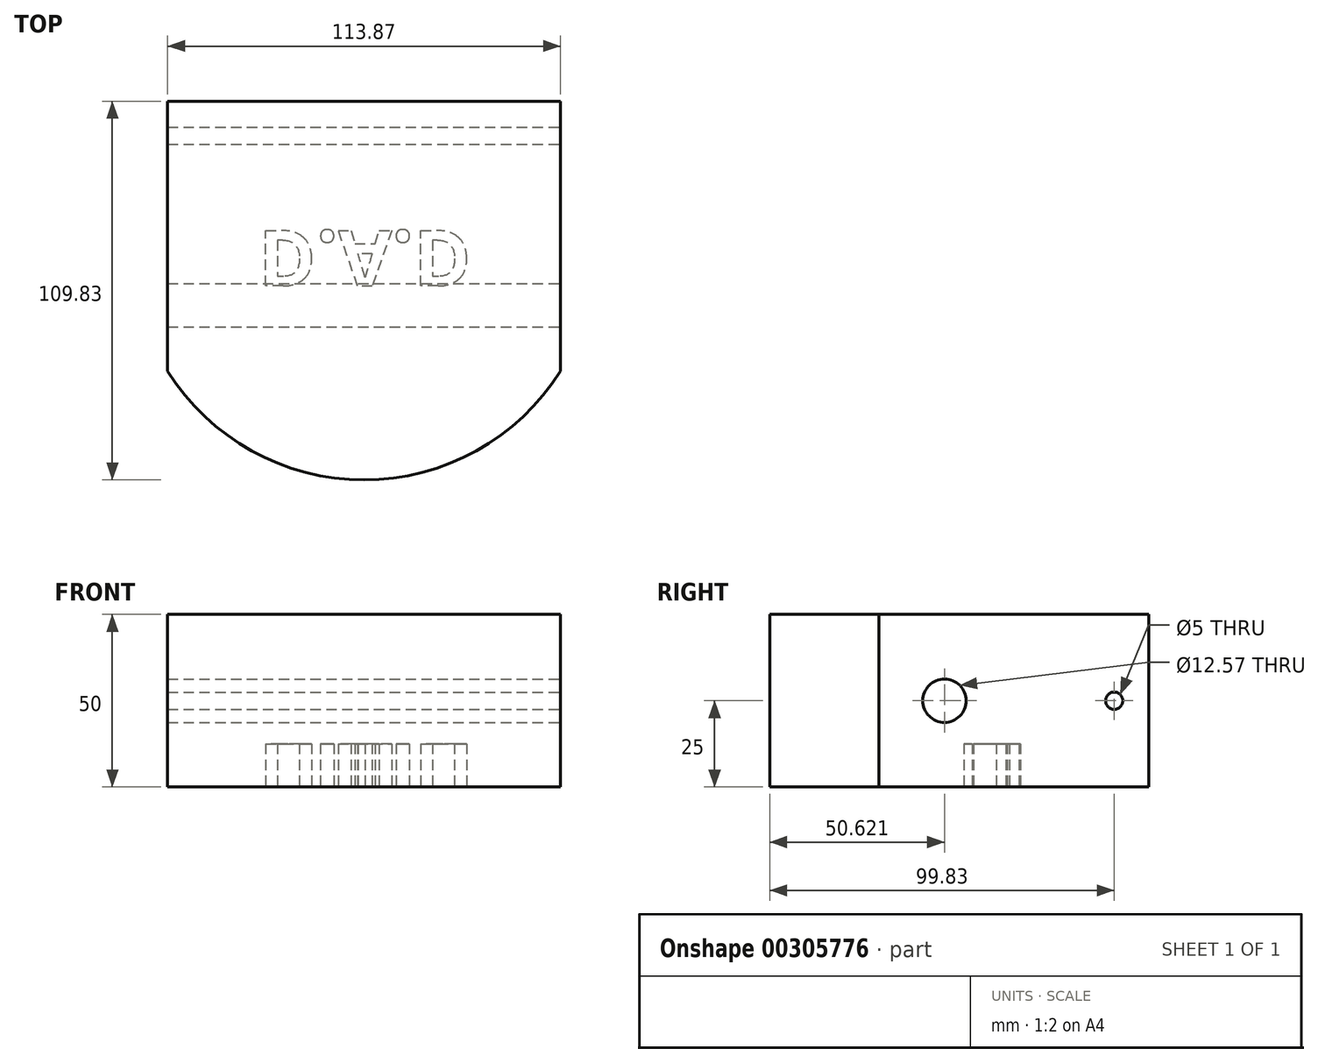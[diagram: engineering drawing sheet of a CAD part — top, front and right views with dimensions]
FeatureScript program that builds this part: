
annotation { "Feature Type Name" : "Feature", "Feature Type Description" : "" }
export const myFeature = defineFeature(function(context is Context, id is Id, definition is map)
    precondition{}
    {
        {
            var Q0;
            Q0=qCreatedBy(makeId("Top.planeOp"),FACE);
            var sketch = newSketch(context, id + "F0", { "sketchPlane" : qUnion([Q0])});
            skLineSegment(sketch, "E0.bottom", {"start": v(56.58, -32.5) * mm, "end": v(-57.29, -32.5) * mm});
            skLineSegment(sketch, "E0.top", {"start": v(56.58, 45.78) * mm, "end": v(-57.29, 45.78) * mm});
            skLineSegment(sketch, "E0.left", {"start": v(56.58, -32.5) * mm, "end": v(56.58, 45.78) * mm});
            skLineSegment(sketch, "E0.right", {"start": v(-57.29, -32.5) * mm, "end": v(-57.29, 45.78) * mm});
            skArc(sketch, "E1", {"start": v(-57.29, -32.5) * mm, "mid": v(-0.35, -64.05) * mm, "end": v(56.58, -32.5) * mm});
            skSolve(sketch);
        }
        {
            var Q0;
            Q0 = qSketchRegion(id + "F0", true);
            extrude(context, id + "F1", {"entities" : qUnion([Q0]), "depth" : 50 * mm});
        }
        {
            var Q0;
            Q0=makeQuery(id+"F1.opExtrude","SWEPT_FACE",FACE,{"disambiguationData":[OSD([sQuery(id+"F0.wireOp",EDGE,"E0.left")])]});
            var sketch = newSketch(context, id + "F2", { "sketchPlane" : qUnion([Q0])});
            skLineSegment(sketch, "E2", {"start": v(45.78, 25) * mm, "end": v(-32.5, 25) * mm, "construction": true});
            skCircle(sketch, "E3", {"center": v(35.78, 25) * mm, "radius": 2.5 * mm});
            skCircle(sketch, "E4", {"center": v(-13.43, 25) * mm, "radius": 6.29 * mm});
            skSolve(sketch);
        }
        {
            var Q0;
            Q0=makeQuery(id+"F2.imprint","IMPRINT",FACE,{"disambiguationData":[TD([[makeQuery(id+"F2.imprint","IMPRINT",EDGE,{"derivedFrom":sQuery(id+"F2.wireOp",EDGE,"E4")}),1.0]])]});
            var Q1;
            Q1=makeQuery(id+"F2.imprint","IMPRINT",FACE,{"disambiguationData":[TD([[makeQuery(id+"F2.imprint","IMPRINT",EDGE,{"derivedFrom":sQuery(id+"F2.wireOp",EDGE,"E3")}),1.0]])]});
            extrude(context, id + "F3", {"entities" : qUnion([Q0, Q1]), "operationType" : NewBodyOperationType.REMOVE, "endBound" : BoundingType.THROUGH_ALL, "oppositeDirection" : true, "depth" : 25 * mm});
        }
        {
            var Q0;
            Q0=makeQuery(id+"F1.opExtrude","CAP_FACE",FACE,{"disambiguationData":[OSD([sQuery(id+"F0.wireOp",EDGE,"E0.top"),sQuery(id+"F0.wireOp",EDGE,"E0.left"),sQuery(id+"F0.wireOp",EDGE,"E0.right"),sQuery(id+"F0.wireOp",EDGE,"E1")])],"isStart":true});
            var sketch = newSketch(context, id + "F4", { "sketchPlane" : qUnion([Q0])});
            skText(sketch, "E5", { "text": "D.A.D", "fontName": "OpenSans-Bold.ttf"});
            skLineSegment(sketch, "E6", {"start": v(0, 64.05) * mm, "end": v(0, -35.17) * mm, "construction": true});
            skLineSegment(sketch, "E7", {"start": v(-57.29, 0) * mm, "end": v(54.39, 0) * mm, "construction": true});
            const initialGuessF4  = {"E5": [-0.03087, -0.00826, 1, 0, 0.01618]};
            skSetInitialGuess(sketch, initialGuessF4);
            skSolve(sketch);
        }
        {
            var Q0;
            Q0 = qSketchRegion(id + "F4", true);
            extrude(context, id + "F5", {"entities" : qUnion([Q0]), "operationType" : NewBodyOperationType.REMOVE, "endBound" : BoundingType.SYMMETRIC, "oppositeDirection" : true, "depth" : 25 * mm});
        }
    });
